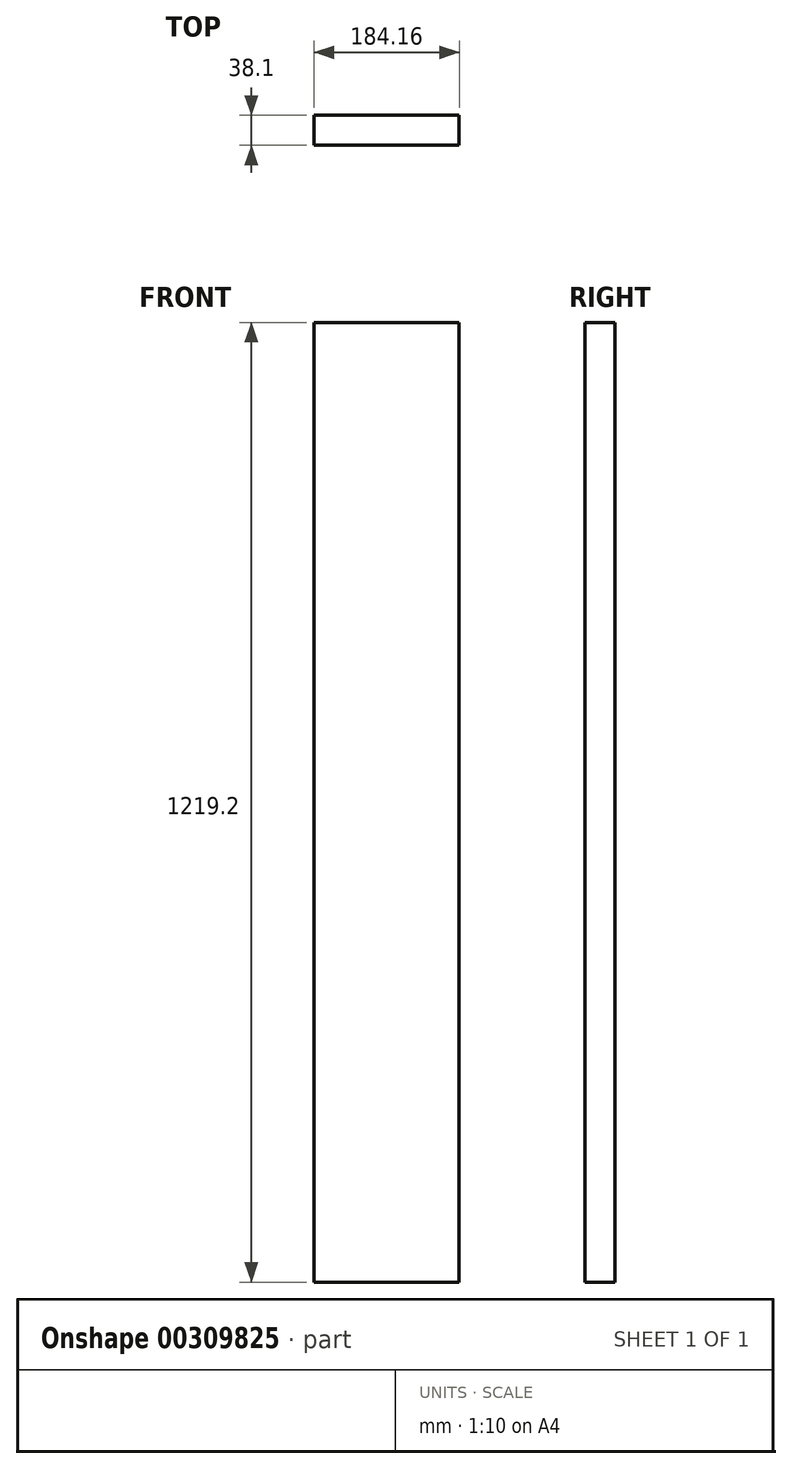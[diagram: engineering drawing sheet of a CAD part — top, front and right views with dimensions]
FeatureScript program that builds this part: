
annotation { "Feature Type Name" : "Feature", "Feature Type Description" : "" }
export const myFeature = defineFeature(function(context is Context, id is Id, definition is map)
    precondition{}
    {
        {
            var Q0;
            Q0=qCreatedBy(makeId("Front.planeOp"),FACE);
            var sketch = newSketch(context, id + "F0", { "sketchPlane" : qUnion([Q0])});
            skLineSegment(sketch, "E0.bottom", {"start": v(92.07, 609.6) * mm, "end": v(-92.08, 609.6) * mm});
            skLineSegment(sketch, "E0.top", {"start": v(92.08, -609.6) * mm, "end": v(-92.07, -609.6) * mm});
            skLineSegment(sketch, "E0.left", {"start": v(92.07, 609.6) * mm, "end": v(92.08, -609.6) * mm});
            skLineSegment(sketch, "E0.right", {"start": v(-92.08, 609.6) * mm, "end": v(-92.07, -609.6) * mm});
            skPoint(sketch, "E0.middle", {"position": v(0, 0) * mm});
            skSolve(sketch);
        }
        {
            var Q0;
            Q0=qSketchRegion(id+"F0",true);
            extrude(context, id + "F1", {"entities" : qUnion([Q0]), "depth" : 38.1 * mm});
        }
    });
